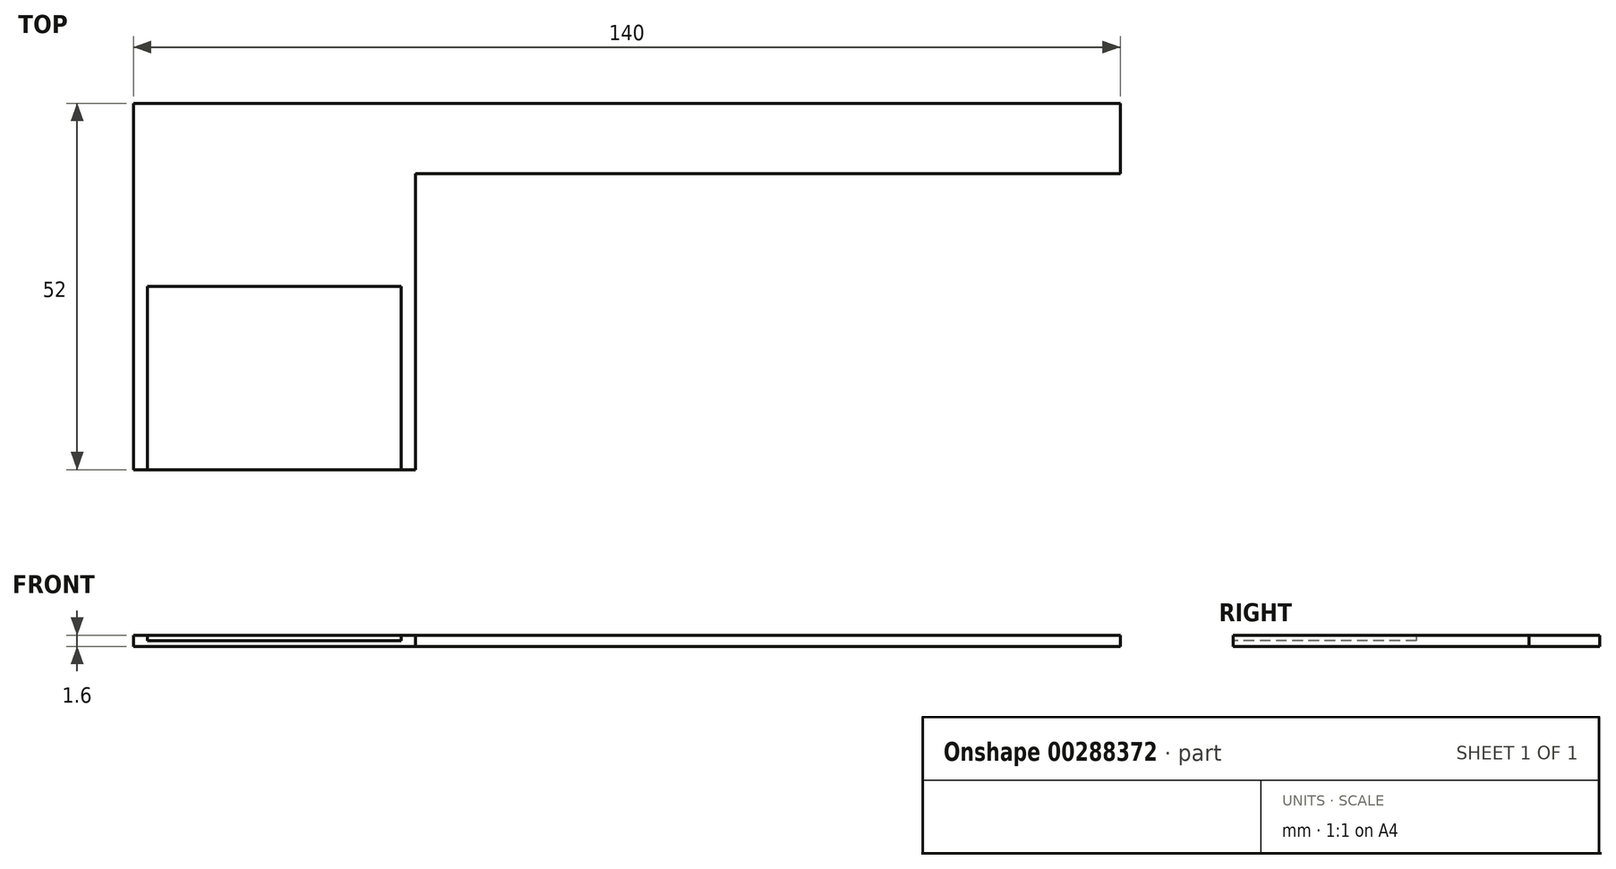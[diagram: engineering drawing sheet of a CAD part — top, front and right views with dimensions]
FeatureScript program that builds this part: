
annotation { "Feature Type Name" : "Feature", "Feature Type Description" : "" }
export const myFeature = defineFeature(function(context is Context, id is Id, definition is map)
    precondition{}
    {
        {
            var Q0;
            Q0=qCreatedBy(makeId("Top.planeOp"),FACE);
            var sketch = newSketch(context, id + "F0", { "sketchPlane" : qUnion([Q0])});
            skLineSegment(sketch, "E0.bottom", {"start": v(0, 0) * mm, "end": v(40, 0) * mm});
            skLineSegment(sketch, "E0.top", {"start": v(0, 52) * mm, "end": v(140, 52) * mm});
            skLineSegment(sketch, "E0.left", {"start": v(0, 0) * mm, "end": v(0, 52) * mm});
            skLineSegment(sketch, "E0.right", {"start": v(140, 42) * mm, "end": v(140, 52) * mm});
            skLineSegment(sketch, "E1", {"start": v(40, 42) * mm, "end": v(140, 42) * mm});
            skLineSegment(sketch, "E2", {"start": v(40, 42) * mm, "end": v(40, 0) * mm});
            skSolve(sketch);
        }
        {
            var Q0;
            Q0 = qSketchRegion(id + "F0", true);
            extrude(context, id + "F1", {"entities" : qUnion([Q0]), "depth" : 0.8 * mm, "offsetDistance" : 25 * mm});
        }
        {
            var Q0;
            Q0=makeQuery(id+"F1.opExtrude","CAP_FACE",FACE,{"disambiguationData":[OSD([sQuery(id+"F0.wireOp",EDGE,"E0.bottom"),sQuery(id+"F0.wireOp",EDGE,"E0.top"),sQuery(id+"F0.wireOp",EDGE,"E0.left"),sQuery(id+"F0.wireOp",EDGE,"E0.right"),sQuery(id+"F0.wireOp",EDGE,"E1"),sQuery(id+"F0.wireOp",EDGE,"E2")])],"isStart":false});
            var sketch = newSketch(context, id + "F2", { "sketchPlane" : qUnion([Q0])});
            skLineSegment(sketch, "E3", {"start": v(2, 0) * mm, "end": v(2, 26) * mm});
            skLineSegment(sketch, "E4", {"start": v(2, 26) * mm, "end": v(38, 26) * mm});
            skLineSegment(sketch, "E5", {"start": v(38, 26) * mm, "end": v(38, 0) * mm});
            skSolve(sketch);
        }
        {
            var Q0;
            Q0 = qSketchRegion(id + "F2", true);
            var Q1;
            {var subQ1=sQuery(id+"F2.wireOp",EDGE,"E3");Q1=makeQuery(id+"F2.imprint","IMPRINT",FACE,{"disambiguationData":[TD([[makeQuery(id+"F2.imprint","IMPRINT",EDGE,{"derivedFrom":subQ1}),1.0]])]});}
            extrude(context, id + "F3", {"entities" : qUnion([Q0, Q1]), "operationType" : NewBodyOperationType.ADD, "depth" : 0.8 * mm, "offsetDistance" : 25 * mm});
        }
    });
